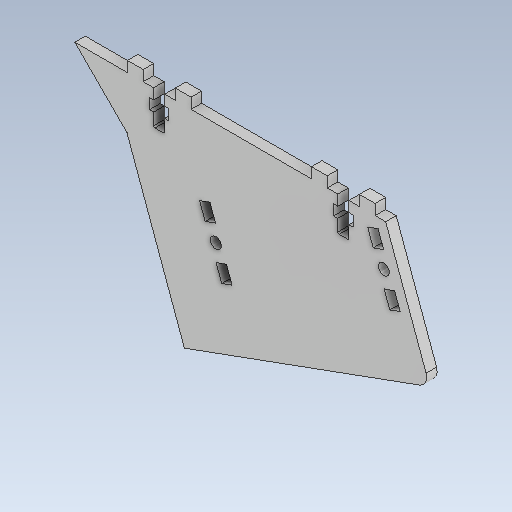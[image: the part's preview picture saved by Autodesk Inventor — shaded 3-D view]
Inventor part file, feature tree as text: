
AUTODESK INVENTOR PART (.ipt)
format: ipt  version: 2020.1 (Build 241239000, 239)  size: 385,536 bytes
history: native  units: mm
features: other x9, extrude x1, sketch x1
ambient origin geometry x8: Origin, YZ Plane, XZ Plane, XY Plane, X Axis, Y Axis, Z Axis, Center Point
bodies: Solide1 (feature_tree)
feature tree (11):
  other  "shared_parameters.ipt"
  other  "tc_base_plate.ipt"
  other  "Blocs"
  extrude  "Extrusion1"  Depth=10.0mm
  other  "Anchor (screw side)"
  other  "Anchor (nut side)"
  sketch  "Esquisse1"
  other  "Anchor (nut side):1"
  other  "Anchor (nut side):2"
  other  "Anchor (screw side):2"
  other  "Anchor (screw side):3"
